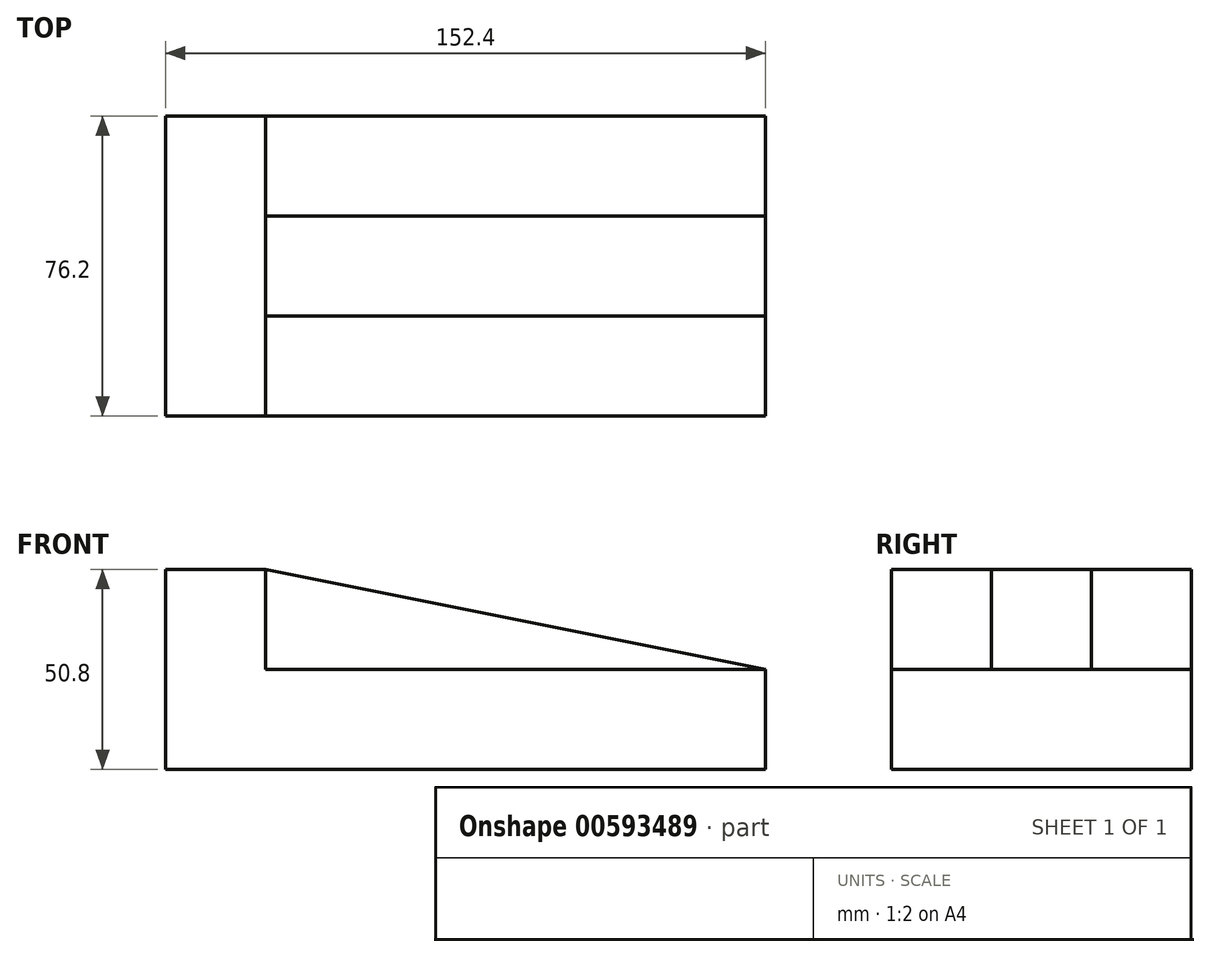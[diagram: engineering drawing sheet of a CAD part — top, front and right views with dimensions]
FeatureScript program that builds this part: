
annotation { "Feature Type Name" : "Feature", "Feature Type Description" : "" }
export const myFeature = defineFeature(function(context is Context, id is Id, definition is map)
    precondition{}
    {
        {
            var Q0;
            Q0=qCreatedBy(makeId("Front.planeOp"),FACE);
            var sketch = newSketch(context, id + "F0", { "sketchPlane" : qUnion([Q0])});
            skLineSegment(sketch, "E0.bottom", {"start": v(0, 0) * mm, "end": v(152.4, 0) * mm});
            skLineSegment(sketch, "E0.top", {"start": v(0, 50.8) * mm, "end": v(152.4, 50.8) * mm});
            skLineSegment(sketch, "E0.left", {"start": v(0, 0) * mm, "end": v(0, 50.8) * mm});
            skLineSegment(sketch, "E0.right", {"start": v(152.4, 0) * mm, "end": v(152.4, 50.8) * mm});
            skSolve(sketch);
        }
        {
            var Q0;
            Q0 = qSketchRegion(id + "F0", true);
            extrude(context, id + "F1", {"entities" : qUnion([Q0]), "depth" : 76.2 * mm, "offsetDistance" : 25.4 * mm});
        }
        {
            var Q0;
            Q0=makeQuery(id+"F1.opExtrude","CAP_FACE",FACE,{"disambiguationData":[OSD([sQuery(id+"F0.wireOp",EDGE,"E0.bottom"),sQuery(id+"F0.wireOp",EDGE,"E0.top"),sQuery(id+"F0.wireOp",EDGE,"E0.left"),sQuery(id+"F0.wireOp",EDGE,"E0.right")])],"isStart":false});
            cPlane(context, id + "F2", {"entities" : qUnion([Q0]), "cplaneType" : CPlaneType.OFFSET, "offset" : 38.1 * mm, "oppositeDirection" : true, "width" : 152.4 * mm, "height" : 152.4 * mm});
        }
        {
            var Q0;
            Q0=makeQuery(id+"F1.opExtrude","CAP_FACE",FACE,{"disambiguationData":[OSD([sQuery(id+"F0.wireOp",EDGE,"E0.bottom"),sQuery(id+"F0.wireOp",EDGE,"E0.top"),sQuery(id+"F0.wireOp",EDGE,"E0.left"),sQuery(id+"F0.wireOp",EDGE,"E0.right")])],"isStart":false});
            cPlane(context, id + "F3", {"entities" : qUnion([Q0]), "cplaneType" : CPlaneType.OFFSET, "offset" : 38.1 * mm, "oppositeDirection" : true, "width" : 152.4 * mm, "height" : 152.4 * mm});
        }
        {
            var Q0;
            Q0=qCreatedBy(id+"F2.planeOp",FACE);
            var sketch = newSketch(context, id + "F4", { "sketchPlane" : qUnion([Q0])});
            skLineSegment(sketch, "E1.top", {"start": v(25.4, 50.8) * mm, "end": v(152.4, 50.8) * mm});
            skLineSegment(sketch, "E2", {"start": v(25.4, 50.8) * mm, "end": v(25.4, 50.8) * mm});
            skLineSegment(sketch, "E3", {"start": v(25.4, 25.4) * mm, "end": v(152.4, 25.4) * mm});
            skLineSegment(sketch, "E4", {"start": v(25.4, 50.8) * mm, "end": v(25.4, 25.4) * mm});
            skLineSegment(sketch, "E5", {"start": v(152.4, 25.4) * mm, "end": v(152.4, 50.8) * mm});
            skPoint(sketch, "E1.right.start.orphan", {"position": v(152.4, 0) * mm});
            skSolve(sketch);
        }
        {
            var Q0;
            Q0 = qSketchRegion(id + "F4", true);
            extrude(context, id + "F5", {"entities" : qUnion([Q0]), "operationType" : NewBodyOperationType.REMOVE, "endBound" : BoundingType.SYMMETRIC, "oppositeDirection" : true, "depth" : 76.2 * mm, "offsetDistance" : 25.4 * mm});
        }
        {
            var Q0;
            Q0=qCreatedBy(id+"F3.planeOp",FACE);
            var sketch = newSketch(context, id + "F6", { "sketchPlane" : qUnion([Q0])});
            skLineSegment(sketch, "E6", {"start": v(25.4, 50.8) * mm, "end": v(25.4, 25.4) * mm});
            skLineSegment(sketch, "E7", {"start": v(25.4, 25.4) * mm, "end": v(152.4, 25.4) * mm});
            skLineSegment(sketch, "E8", {"start": v(25.4, 50.8) * mm, "end": v(25.4, 50.8) * mm});
            skLineSegment(sketch, "E9", {"start": v(25.4, 50.8) * mm, "end": v(152.4, 25.4) * mm});
            skPoint(sketch, "E10.end.orphan", {"position": v(152.4, 50.8) * mm});
            skPoint(sketch, "E11.right.end.orphan", {"position": v(152.4, 25.4) * mm});
            skPoint(sketch, "E11.bottom.end.orphan", {"position": v(152.4, 0) * mm});
            skSolve(sketch);
        }
        {
            var Q0;
            Q0 = qSketchRegion(id + "F6", true);
            extrude(context, id + "F7", {"entities" : qUnion([Q0]), "operationType" : NewBodyOperationType.ADD, "endBound" : BoundingType.SYMMETRIC, "depth" : 25.4 * mm, "offsetDistance" : 25.4 * mm});
        }
    });
